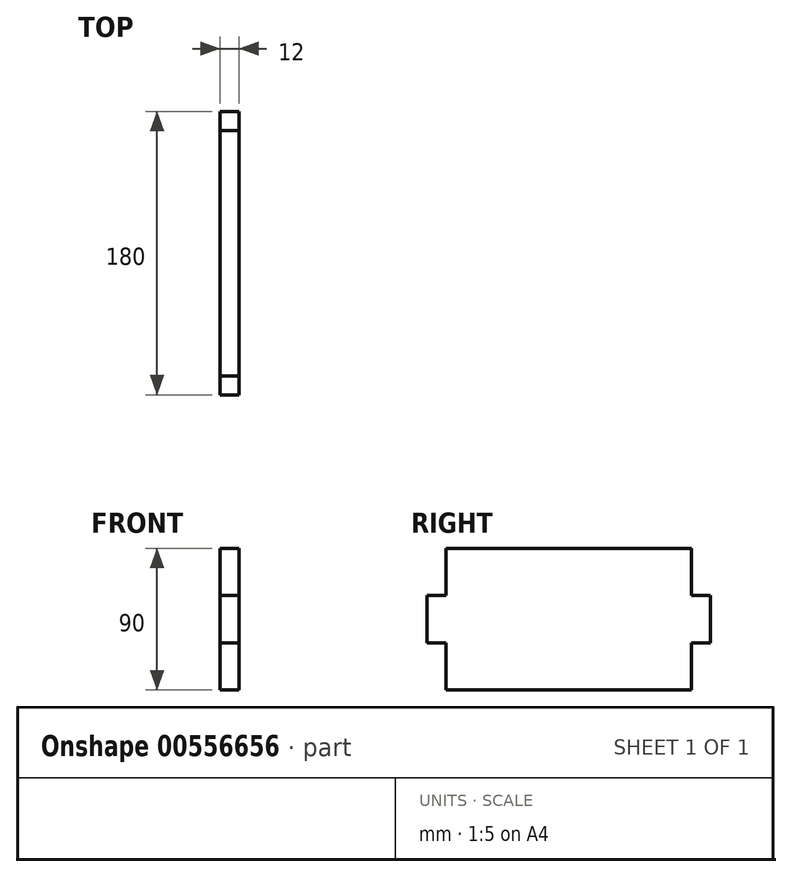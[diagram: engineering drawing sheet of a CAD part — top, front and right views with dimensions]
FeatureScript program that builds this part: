
annotation { "Feature Type Name" : "Feature", "Feature Type Description" : "" }
export const myFeature = defineFeature(function(context is Context, id is Id, definition is map)
    precondition{}
    {
        {
            var Q0;
            Q0=qCreatedBy(makeId("Right.planeOp"),FACE);
            var sketch = newSketch(context, id + "F0", { "sketchPlane" : qUnion([Q0])});
            skLineSegment(sketch, "E0", {"start": v(0, 0) * mm, "end": v(0, 30) * mm});
            skLineSegment(sketch, "E1", {"start": v(0, 30) * mm, "end": v(-12, 30) * mm});
            skLineSegment(sketch, "E2", {"start": v(-12, 30) * mm, "end": v(-12, 60) * mm});
            skLineSegment(sketch, "E3", {"start": v(-12, 60) * mm, "end": v(0, 60) * mm});
            skLineSegment(sketch, "E4", {"start": v(0, 60) * mm, "end": v(0, 90) * mm});
            skLineSegment(sketch, "E5", {"start": v(0, 90) * mm, "end": v(78, 90) * mm});
            skLineSegment(sketch, "E6", {"start": v(78, 90) * mm, "end": v(78, 0) * mm, "construction": true});
            skLineSegment(sketch, "E7", {"start": v(78, 0) * mm, "end": v(-1.63, 0) * mm});
            skLineSegment(sketch, "E8.MirrorCS", {"start": v(156, 0) * mm, "end": v(156, 30) * mm});
            skLineSegment(sketch, "E9.MirrorCS", {"start": v(156, 30) * mm, "end": v(168, 30) * mm});
            skLineSegment(sketch, "E10.MirrorCS", {"start": v(168, 60) * mm, "end": v(156, 60) * mm});
            skLineSegment(sketch, "E11.MirrorCS", {"start": v(156, 60) * mm, "end": v(156, 90) * mm});
            skLineSegment(sketch, "E12.MirrorCS", {"start": v(78, 0) * mm, "end": v(157.63, 0) * mm});
            skLineSegment(sketch, "E13.MirrorCS", {"start": v(156, 90) * mm, "end": v(78, 90) * mm});
            skLineSegment(sketch, "E14.MirrorCS", {"start": v(168, 30) * mm, "end": v(168, 60) * mm});
            skSolve(sketch);
        }
        {
            var Q0;
            {var subQ2=sQuery(id+"F0.wireOp",EDGE,"E0");Q0=makeQuery(id+"F0.imprint","IMPRINT",FACE,{"disambiguationData":[TD([[makeQuery(id+"F0.imprint","IMPRINT",EDGE,{"derivedFrom":subQ2}),-1.0]])]});}
            extrude(context, id + "F1", {"entities" : qUnion([Q0]), "endBound" : BoundingType.SYMMETRIC, "depth" : 12 * mm, "offsetDistance" : 25 * mm});
        }
    });
